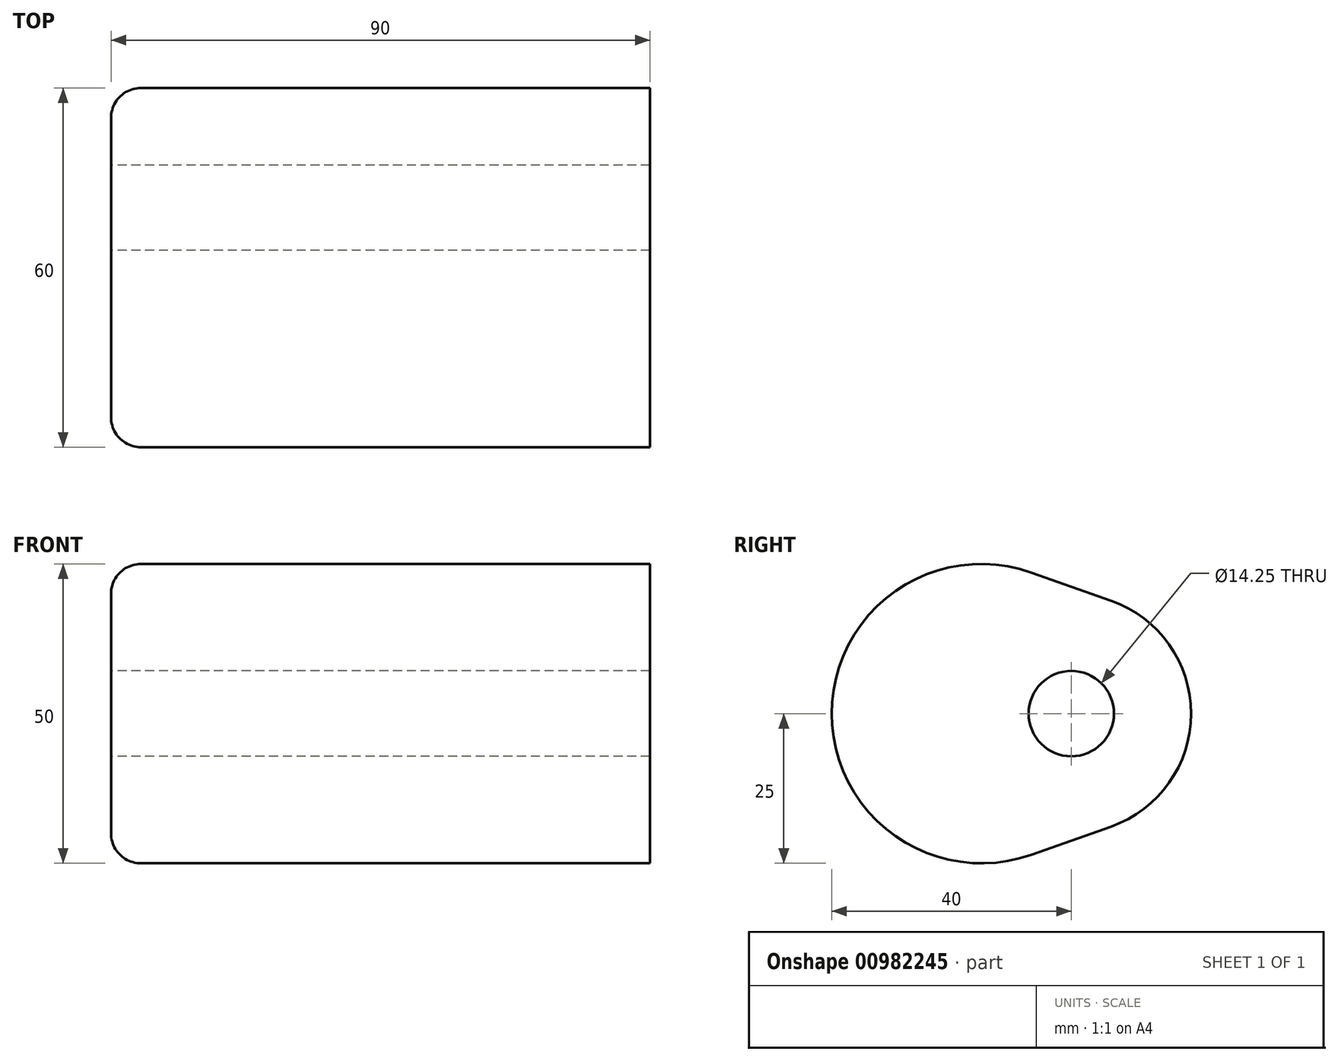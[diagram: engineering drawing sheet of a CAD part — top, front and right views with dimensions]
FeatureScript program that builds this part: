
annotation { "Feature Type Name" : "Feature", "Feature Type Description" : "" }
export const myFeature = defineFeature(function(context is Context, id is Id, definition is map)
    precondition{}
    {
        {
            var Q0;
            Q0=qCreatedBy(makeId("Right.planeOp"),FACE);
            var sketch = newSketch(context, id + "F0", { "sketchPlane" : qUnion([Q0])});
            skCircle(sketch, "E0", {"center": v(0, 0) * mm, "radius": 7.12 * mm});
            skArc(sketch, "E1", {"start": v(-6.67, 23.57) * mm, "mid": v(-40, 0) * mm, "end": v(-6.67, -23.57) * mm});
            skArc(sketch, "E2", {"start": v(6.67, -18.86) * mm, "mid": v(20, 0) * mm, "end": v(6.67, 18.86) * mm});
            skLineSegment(sketch, "E3", {"start": v(-6.67, 23.57) * mm, "end": v(6.67, 18.86) * mm});
            skLineSegment(sketch, "E4", {"start": v(-6.67, -23.57) * mm, "end": v(6.67, -18.86) * mm});
            skSolve(sketch);
        }
        {
            var Q0;
            Q0 = qSketchRegion(id + "F0", true);
            extrude(context, id + "F1", {"entities" : qUnion([Q0]), "endBound" : BoundingType.SYMMETRIC, "depth" : 90 * mm, "offsetDistance" : 25 * mm});
        }
        {
            var Q0;
            Q0=makeQuery(id+"F1.opExtrude","CAP_EDGE",EDGE,{"disambiguationData":[OSD([sQuery(id+"F0.wireOp",EDGE,"E1")])],"isStart":true});
            fillet(context, id + "F2", {"entities" : qUnion([Q0]), "radius" : 5 * mm, "tangentPropagation" : true, "allowEdgeOverflow" : false});
        }
    });
